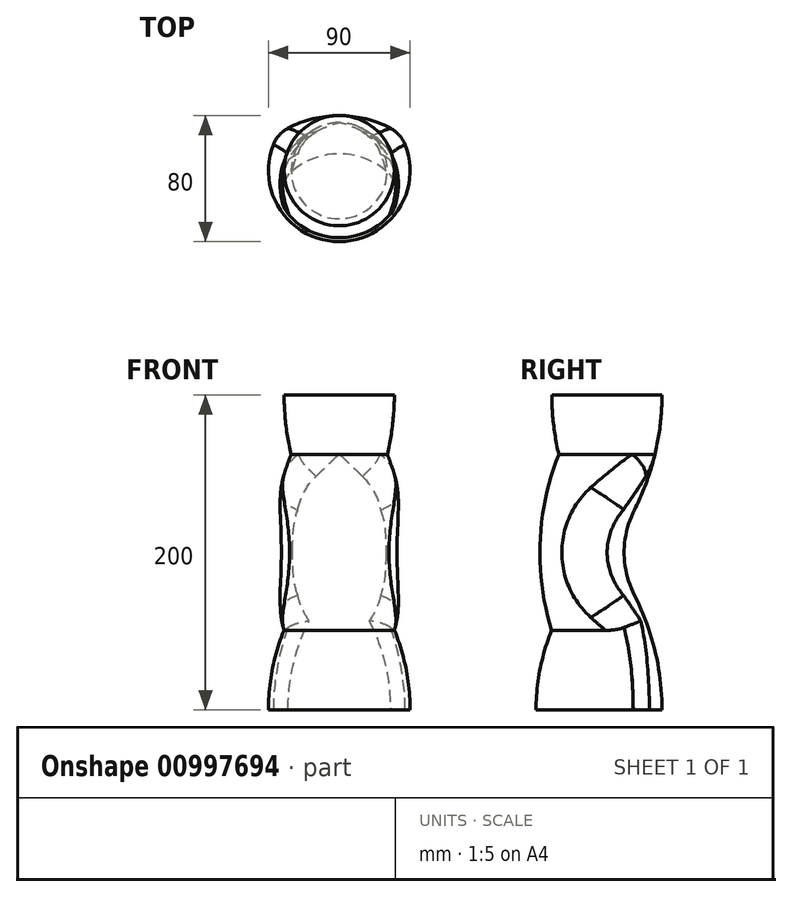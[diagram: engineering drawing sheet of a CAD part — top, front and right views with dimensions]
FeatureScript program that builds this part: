
annotation { "Feature Type Name" : "Feature", "Feature Type Description" : "" }
export const myFeature = defineFeature(function(context is Context, id is Id, definition is map)
    precondition{}
    {
        {
            var Q0;
            Q0=qCreatedBy(makeId("Top.planeOp"),FACE);
            var sketch = newSketch(context, id + "F0", { "sketchPlane" : qUnion([Q0])});
            skCircle(sketch, "E0", {"center": v(0, 0) * mm, "radius": 35 * mm});
            skLineSegment(sketch, "E1", {"start": v(-35, 0) * mm, "end": v(35, 0) * mm, "construction": true});
            skEllipse(sketch, "E2", {"center": v(0, 0) * mm, "majorRadius": 45 * mm, "minorRadius": 35 * mm, "majorAxis": v(0, -1)});
            skArc(sketch, "E3", {"start": v(60.62, 0) * mm, "mid": v(0, 35) * mm, "end": v(-60.62, 0) * mm});
            skLineSegment(sketch, "E4", {"start": v(-60.62, 0) * mm, "end": v(60.62, 0) * mm});
            skPoint(sketch, "E5", {"position": v(0, -45) * mm});
            skSolve(sketch);
        }
        {
            var Q0;
            Q0=qCreatedBy(makeId("Right.planeOp"),FACE);
            var sketch = newSketch(context, id + "F1", { "sketchPlane" : qUnion([Q0])});
            skLineSegment(sketch, "E6", {"start": v(-45, 0) * mm, "end": v(35, 0) * mm});
            skArc(sketch, "E7", {"start": v(-45, 0) * mm, "mid": v(-33.23, 54.83) * mm, "end": v(0, 100) * mm});
            skArc(sketch, "E8", {"start": v(35, 0) * mm, "mid": v(30.56, 37.46) * mm, "end": v(17.5, 72.84) * mm});
            skLineSegment(sketch, "E9", {"start": v(0, 100) * mm, "end": v(0, 0) * mm});
            skLineSegment(sketch, "E10", {"start": v(-35, 200) * mm, "end": v(35, 200) * mm});
            skArc(sketch, "E11", {"start": v(-35, 200) * mm, "mid": v(-26, 147.03) * mm, "end": v(0, 100) * mm});
            skArc(sketch, "E12", {"start": v(35, 200) * mm, "mid": v(26, 147.03) * mm, "end": v(0, 100) * mm});
            skArc(sketch, "E13", {"start": v(17.5, 72.84) * mm, "mid": v(10.98, 100) * mm, "end": v(17.5, 127.16) * mm});
            skArc(sketch, "E14", {"start": v(-30.5, 162.3) * mm, "mid": v(-42.43, 106.81) * mm, "end": v(-35.07, 50.54) * mm});
            skLineSegment(sketch, "E15", {"start": v(0, 100) * mm, "end": v(0, 200) * mm});
            skLineSegment(sketch, "E16", {"start": v(35, 200) * mm, "end": v(35, 0) * mm});
            skLineSegment(sketch, "E17.bottom", {"start": v(35, 0) * mm, "end": v(70.13, 0) * mm});
            skLineSegment(sketch, "E17.top", {"start": v(35, 200) * mm, "end": v(70.13, 200) * mm});
            skLineSegment(sketch, "E17.left", {"start": v(35, 0) * mm, "end": v(35, 200) * mm});
            skLineSegment(sketch, "E17.right", {"start": v(70.13, 0) * mm, "end": v(70.13, 200) * mm});
            skSolve(sketch);
        }
        {
            var Q0;
            {var subQ3=sQuery(id+"F1.wireOp",EDGE,"E15");Q0=makeQuery(id+"F1.imprint","IMPRINT",FACE,{"disambiguationData":[TD([[makeQuery(id+"F1.imprint","IMPRINT",EDGE,{"derivedFrom":subQ3}),1.0]])]});}
            var Q1;
            {var subQ3=sQuery(id+"F1.wireOp",EDGE,"E14");Q1=makeQuery(id+"F1.imprint","IMPRINT",FACE,{"disambiguationData":[TD([[makeQuery(id+"F1.imprint","IMPRINT",EDGE,{"derivedFrom":subQ3}),1.0]])]});}
            var Q2;
            {var subQ3=sQuery(id+"F1.wireOp",EDGE,"E9");Q2=makeQuery(id+"F1.imprint","IMPRINT",FACE,{"disambiguationData":[TD([[makeQuery(id+"F1.imprint","IMPRINT",EDGE,{"derivedFrom":subQ3}),-1.0]])]});}
            var Q3;
            Q3=sQuery(id+"F1.wireOp",EDGE,"E15");
            revolve(context, id + "F2", {"surfaceOperationType" : NewSurfaceOperationType.NEW, "entities" : qUnion([Q0, Q1, Q2]), "axis" : qUnion([Q3]), "revolveType" : RevolveType.FULL});
        }
        {
            var Q0;
            Q0=makeQuery(id+"F1.imprint","IMPRINT",FACE,{"disambiguationData":[TD([[makeQuery(id+"F1.imprint","IMPRINT",EDGE,{"derivedFrom":sQuery(id+"F1.wireOp",EDGE,"E8")}),-1.0]])]});
            var Q1;
            Q1=makeQuery(id+"F1.imprint","IMPRINT",FACE,{"disambiguationData":[TD([[makeQuery(id+"F1.imprint","IMPRINT",EDGE,{"derivedFrom":sQuery(id+"F1.wireOp",EDGE,"E17.bottom")}),1.0]])]});
            var Q2;
            Q2=sQuery(id+"F0.wireOp",EDGE,"E3");
            sweep(context, id + "F3", {"operationType" : NewBodyOperationType.REMOVE, "profiles" : qUnion([Q0, Q1]), "path" : qUnion([Q2])});
        }
        {
            var Q0;
            Q0=makeQuery(id+"F3.boolean.opBoolean","INTERSECT",EDGE,{"disambiguationData":[OD(0.0)],"derivedFrom":[makeQuery(id+"F2.opRevolve","SWEPT_FACE",FACE,{"disambiguationData":[OSD([sQuery(id+"F1.wireOp",EDGE,"E7")])]}),makeQuery(id+"F3.opSweep","SWEPT_FACE",FACE,{"disambiguationData":[OSD([sQuery(id+"F0.wireOp",EDGE,"E3"),sQuery(id+"F1.wireOp",EDGE,"E8")])]})]});
            var Q1;
            Q1=makeQuery(id+"F3.boolean.opBoolean","INTERSECT",EDGE,{"disambiguationData":[OD(0.0)],"derivedFrom":[makeQuery(id+"F2.opRevolve","SWEPT_FACE",FACE,{"disambiguationData":[OSD([sQuery(id+"F1.wireOp",EDGE,"E14")])]}),makeQuery(id+"F3.opSweep","SWEPT_FACE",FACE,{"disambiguationData":[OSD([sQuery(id+"F0.wireOp",EDGE,"E3"),sQuery(id+"F1.wireOp",EDGE,"E8")])]})]});
            var Q2;
            Q2=makeQuery(id+"F3.boolean.opBoolean","COPY",FACE,{"derivedFrom":makeQuery(id+"F3.opSweep","SWEPT_FACE",FACE,{"disambiguationData":[OSD([sQuery(id+"F0.wireOp",EDGE,"E3"),sQuery(id+"F1.wireOp",EDGE,"E13")])]})});
            var Q3;
            Q3=makeQuery(id+"F3.boolean.opBoolean","COPY",FACE,{"derivedFrom":makeQuery(id+"F3.opSweep","SWEPT_FACE",FACE,{"disambiguationData":[OSD([sQuery(id+"F0.wireOp",EDGE,"E3"),sQuery(id+"F1.wireOp",EDGE,"E12")])]})});
            var Q4;
            Q4=makeQuery(id+"F3.boolean.opBoolean","INTERSECT",EDGE,{"disambiguationData":[OD(1.0)],"derivedFrom":[makeQuery(id+"F2.opRevolve","SWEPT_FACE",FACE,{"disambiguationData":[OSD([sQuery(id+"F1.wireOp",EDGE,"E7")])]}),makeQuery(id+"F3.opSweep","SWEPT_FACE",FACE,{"disambiguationData":[OSD([sQuery(id+"F0.wireOp",EDGE,"E3"),sQuery(id+"F1.wireOp",EDGE,"E8")])]})]});
            var Q5;
            Q5=makeQuery(id+"F3.boolean.opBoolean","INTERSECT",EDGE,{"disambiguationData":[OD(1.0)],"derivedFrom":[makeQuery(id+"F2.opRevolve","SWEPT_FACE",FACE,{"disambiguationData":[OSD([sQuery(id+"F1.wireOp",EDGE,"E14")])]}),makeQuery(id+"F3.opSweep","SWEPT_FACE",FACE,{"disambiguationData":[OSD([sQuery(id+"F0.wireOp",EDGE,"E3"),sQuery(id+"F1.wireOp",EDGE,"E8")])]})]});
            fillet(context, id + "F4", {"entities" : qUnion([Q0, Q1, Q2, Q3, Q4, Q5]), "radius" : 20 * mm, "tangentPropagation" : true, "allowEdgeOverflow" : false});
        }
    });
